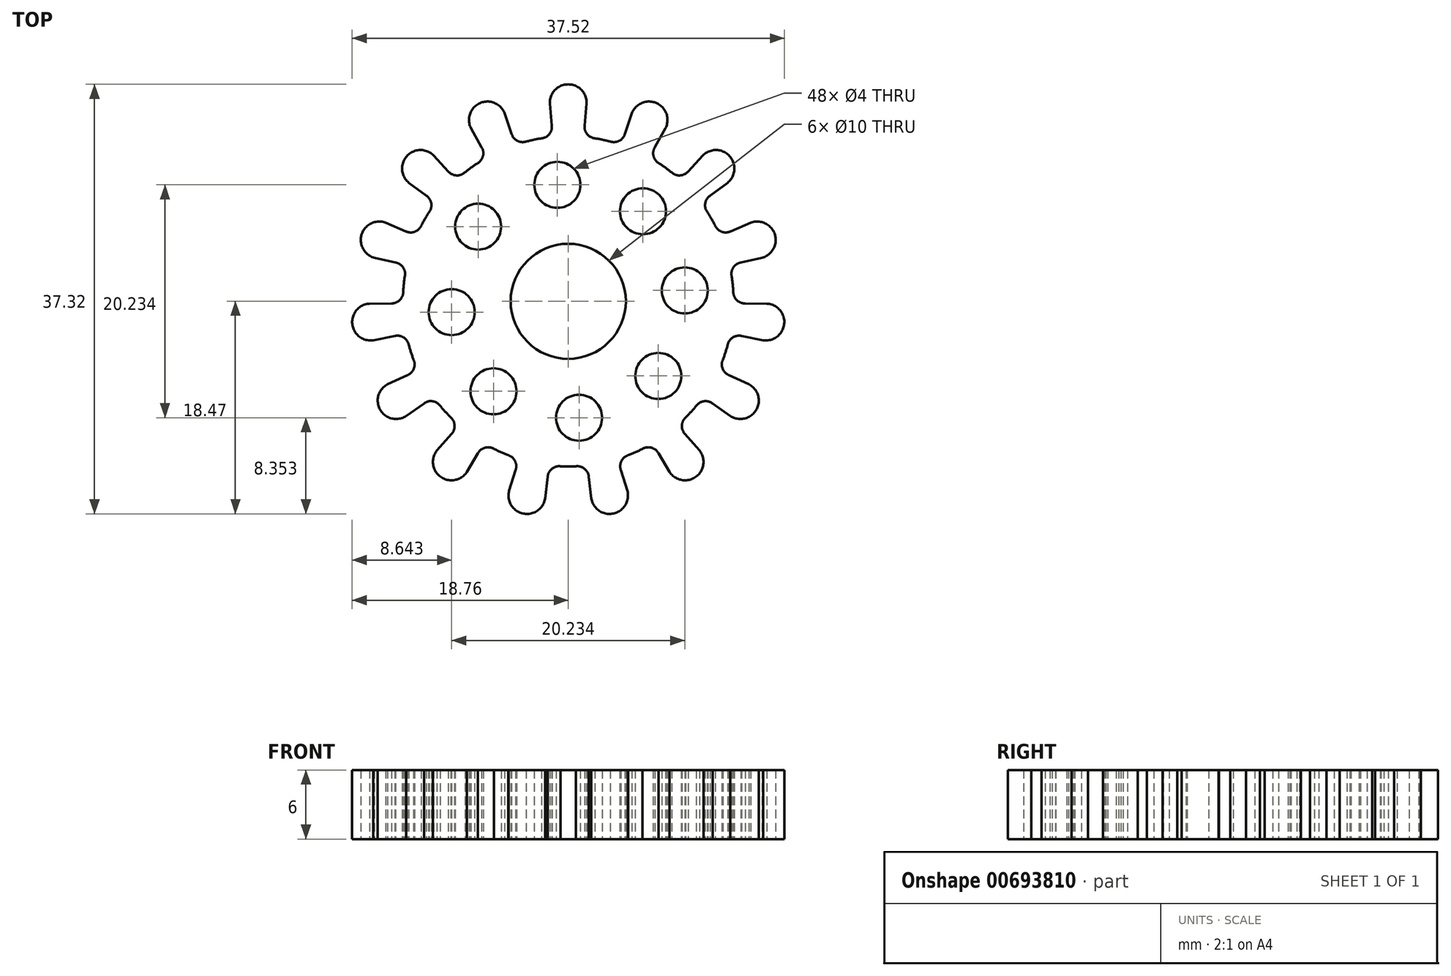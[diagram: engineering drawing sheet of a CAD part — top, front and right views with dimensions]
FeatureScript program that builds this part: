
annotation { "Feature Type Name" : "Feature", "Feature Type Description" : "" }
export const myFeature = defineFeature(function(context is Context, id is Id, definition is map)
    precondition{}
    {
        {
            var Q0;
            Q0=qCreatedBy(makeId("Top.planeOp"),FACE);
            var sketch = newSketch(context, id + "F0", { "sketchPlane" : qUnion([Q0])});
            skArc(sketch, "E0", {"start": v(1.6, 17.18) * mm, "mid": v(0, 18.85) * mm, "end": v(-1.6, 17.18) * mm});
            skPoint(sketch, "E1.center", {"position": v(0, 0) * mm});
            skLineSegment(sketch, "E2", {"start": v(1.6, 17.18) * mm, "end": v(1.42, 15.29) * mm});
            skArc(sketch, "E3", {"start": v(1.42, 15.29) * mm, "mid": v(1.63, 14.53) * mm, "end": v(2.32, 14.16) * mm});
            skCircle(sketch, "E4", {"center": v(0, 0) * mm, "radius": 17.25 * mm, "construction": true});
            skLineSegment(sketch, "E5.anchor1", {"start": v(0, 0) * mm, "end": v(-1.6, 17.18) * mm, "construction": true});
            skArc(sketch, "E6", {"start": v(3.64, 13.88) * mm, "mid": v(4.42, 13.94) * mm, "end": v(4.92, 14.54) * mm});
            skLineSegment(sketch, "E7", {"start": v(4.92, 14.54) * mm, "end": v(5.53, 16.34) * mm});
            skArc(sketch, "E8", {"start": v(2.32, 14.16) * mm, "mid": v(2.98, 14.04) * mm, "end": v(3.64, 13.88) * mm});
            skArc(sketch, "E9.1.0", {"start": v(8.45, 15.04) * mm, "mid": v(7.67, 17.22) * mm, "end": v(5.53, 16.34) * mm});
            skPoint(sketch, "E9.1.1", {"position": v(7.02, 15.76) * mm});
            skArc(sketch, "E9.1.2", {"start": v(8.97, 11.2) * mm, "mid": v(9.7, 10.94) * mm, "end": v(10.4, 11.28) * mm});
            skLineSegment(sketch, "E9.1.3", {"start": v(10.4, 11.28) * mm, "end": v(11.7, 12.68) * mm});
            skLineSegment(sketch, "E9.1.4", {"start": v(8.45, 15.04) * mm, "end": v(7.52, 13.39) * mm});
            skArc(sketch, "E9.1.5", {"start": v(7.52, 13.39) * mm, "mid": v(7.4, 12.61) * mm, "end": v(7.88, 12) * mm});
            skArc(sketch, "E9.1.6", {"start": v(7.88, 12) * mm, "mid": v(8.43, 11.6) * mm, "end": v(8.97, 11.2) * mm});
            skArc(sketch, "E9.2.0", {"start": v(13.83, 10.3) * mm, "mid": v(14, 12.61) * mm, "end": v(11.7, 12.68) * mm});
            skPoint(sketch, "E9.2.1", {"position": v(12.82, 11.54) * mm});
            skArc(sketch, "E9.2.2", {"start": v(12.75, 6.58) * mm, "mid": v(13.32, 6.04) * mm, "end": v(14.1, 6.08) * mm});
            skLineSegment(sketch, "E9.2.3", {"start": v(14.1, 6.08) * mm, "end": v(15.84, 6.83) * mm});
            skLineSegment(sketch, "E9.2.4", {"start": v(13.83, 10.3) * mm, "end": v(12.31, 9.17) * mm});
            skArc(sketch, "E9.2.5", {"start": v(12.31, 9.17) * mm, "mid": v(11.9, 8.51) * mm, "end": v(12.08, 7.75) * mm});
            skArc(sketch, "E9.2.6", {"start": v(12.08, 7.75) * mm, "mid": v(12.43, 7.17) * mm, "end": v(12.75, 6.58) * mm});
            skArc(sketch, "E9.3.0", {"start": v(16.83, 3.79) * mm, "mid": v(17.93, 5.82) * mm, "end": v(15.84, 6.83) * mm});
            skPoint(sketch, "E9.3.1", {"position": v(16.4, 5.33) * mm});
            skArc(sketch, "E9.3.2", {"start": v(14.33, 0.83) * mm, "mid": v(14.62, 0.1) * mm, "end": v(15.35, -0.18) * mm});
            skLineSegment(sketch, "E9.3.3", {"start": v(15.35, -0.18) * mm, "end": v(17.25, -0.2) * mm});
            skLineSegment(sketch, "E9.3.4", {"start": v(16.83, 3.79) * mm, "end": v(14.98, 3.37) * mm});
            skArc(sketch, "E9.3.5", {"start": v(14.98, 3.37) * mm, "mid": v(14.33, 2.94) * mm, "end": v(14.19, 2.17) * mm});
            skArc(sketch, "E9.3.6", {"start": v(14.19, 2.17) * mm, "mid": v(14.27, 1.5) * mm, "end": v(14.33, 0.83) * mm});
            skArc(sketch, "E9.4.0", {"start": v(16.91, -3.38) * mm, "mid": v(18.75, -1.97) * mm, "end": v(17.25, -0.2) * mm});
            skPoint(sketch, "E9.4.1", {"position": v(17.16, -1.8) * mm});
            skArc(sketch, "E9.4.2", {"start": v(13.42, -5.07) * mm, "mid": v(13.4, -5.85) * mm, "end": v(13.95, -6.41) * mm});
            skLineSegment(sketch, "E9.4.3", {"start": v(13.95, -6.41) * mm, "end": v(15.67, -7.2) * mm});
            skLineSegment(sketch, "E9.4.4", {"start": v(16.91, -3.38) * mm, "end": v(15.06, -3.01) * mm});
            skArc(sketch, "E9.4.5", {"start": v(15.06, -3.01) * mm, "mid": v(14.28, -3.14) * mm, "end": v(13.84, -3.79) * mm});
            skArc(sketch, "E9.4.6", {"start": v(13.84, -3.79) * mm, "mid": v(13.65, -4.43) * mm, "end": v(13.42, -5.07) * mm});
            skArc(sketch, "E9.5.0", {"start": v(14.08, -9.97) * mm, "mid": v(16.32, -9.43) * mm, "end": v(15.67, -7.2) * mm});
            skPoint(sketch, "E9.5.1", {"position": v(14.94, -8.63) * mm});
            skArc(sketch, "E9.5.2", {"start": v(10.2, -10.1) * mm, "mid": v(9.86, -10.8) * mm, "end": v(10.13, -11.53) * mm});
            skLineSegment(sketch, "E9.5.3", {"start": v(10.13, -11.53) * mm, "end": v(11.39, -12.96) * mm});
            skLineSegment(sketch, "E9.5.4", {"start": v(14.08, -9.97) * mm, "end": v(12.53, -8.88) * mm});
            skArc(sketch, "E9.5.5", {"start": v(12.53, -8.88) * mm, "mid": v(11.77, -8.68) * mm, "end": v(11.1, -9.1) * mm});
            skArc(sketch, "E9.5.6", {"start": v(11.1, -9.1) * mm, "mid": v(10.66, -9.6) * mm, "end": v(10.2, -10.1) * mm});
            skArc(sketch, "E9.6.0", {"start": v(8.8, -14.83) * mm, "mid": v(11.08, -15.25) * mm, "end": v(11.39, -12.96) * mm});
            skPoint(sketch, "E9.6.1", {"position": v(10.14, -13.96) * mm});
            skArc(sketch, "E9.6.2", {"start": v(5.21, -13.37) * mm, "mid": v(4.62, -13.87) * mm, "end": v(4.57, -14.65) * mm});
            skLineSegment(sketch, "E9.6.3", {"start": v(4.57, -14.65) * mm, "end": v(5.13, -16.47) * mm});
            skLineSegment(sketch, "E9.6.4", {"start": v(8.8, -14.83) * mm, "end": v(7.84, -13.2) * mm});
            skArc(sketch, "E9.6.5", {"start": v(7.84, -13.2) * mm, "mid": v(7.22, -12.72) * mm, "end": v(6.45, -12.82) * mm});
            skArc(sketch, "E9.6.6", {"start": v(6.45, -12.82) * mm, "mid": v(5.84, -13.1) * mm, "end": v(5.21, -13.37) * mm});
            skArc(sketch, "E9.7.0", {"start": v(2, -17.13) * mm, "mid": v(3.92, -18.44) * mm, "end": v(5.13, -16.47) * mm});
            skPoint(sketch, "E9.7.1", {"position": v(3.59, -16.87) * mm});
            skArc(sketch, "E9.7.2", {"start": v(-0.67, -14.33) * mm, "mid": v(-1.42, -14.55) * mm, "end": v(-1.79, -15.25) * mm});
            skLineSegment(sketch, "E9.7.3", {"start": v(-1.79, -15.25) * mm, "end": v(-2, -17.13) * mm});
            skLineSegment(sketch, "E9.7.4", {"start": v(2, -17.13) * mm, "end": v(1.79, -15.25) * mm});
            skArc(sketch, "E9.7.5", {"start": v(1.79, -15.25) * mm, "mid": v(1.43, -14.56) * mm, "end": v(0.67, -14.33) * mm});
            skArc(sketch, "E9.7.6", {"start": v(0.67, -14.33) * mm, "mid": v(0, -14.35) * mm, "end": v(-0.67, -14.33) * mm});
            skArc(sketch, "E9.8.0", {"start": v(-5.13, -16.47) * mm, "mid": v(-3.92, -18.44) * mm, "end": v(-2, -17.13) * mm});
            skPoint(sketch, "E9.8.1", {"position": v(-3.59, -16.87) * mm});
            skArc(sketch, "E9.8.2", {"start": v(-6.45, -12.82) * mm, "mid": v(-7.22, -12.72) * mm, "end": v(-7.83, -13.2) * mm});
            skLineSegment(sketch, "E9.8.3", {"start": v(-7.83, -13.2) * mm, "end": v(-8.8, -14.83) * mm});
            skLineSegment(sketch, "E9.8.4", {"start": v(-5.13, -16.47) * mm, "end": v(-4.57, -14.66) * mm});
            skArc(sketch, "E9.8.5", {"start": v(-4.57, -14.66) * mm, "mid": v(-4.62, -13.88) * mm, "end": v(-5.21, -13.37) * mm});
            skArc(sketch, "E9.8.6", {"start": v(-5.21, -13.37) * mm, "mid": v(-5.84, -13.1) * mm, "end": v(-6.45, -12.82) * mm});
            skLineSegment(sketch, "E9.anchor2", {"start": v(0, 0) * mm, "end": v(-2, -17.13) * mm, "construction": true});
            skArc(sketch, "E10.1.0", {"start": v(-11.39, -12.96) * mm, "mid": v(-11.08, -15.25) * mm, "end": v(-8.8, -14.83) * mm});
            skLineSegment(sketch, "E10.1.1", {"start": v(-11.39, -12.96) * mm, "end": v(-10.14, -11.53) * mm});
            skArc(sketch, "E10.1.2", {"start": v(-10.14, -11.53) * mm, "mid": v(-9.86, -10.8) * mm, "end": v(-10.2, -10.1) * mm});
            skArc(sketch, "E10.1.3", {"start": v(-10.2, -10.1) * mm, "mid": v(-10.66, -9.6) * mm, "end": v(-11.1, -9.1) * mm});
            skArc(sketch, "E10.1.4", {"start": v(-11.1, -9.1) * mm, "mid": v(-11.77, -8.68) * mm, "end": v(-12.53, -8.87) * mm});
            skLineSegment(sketch, "E10.1.5", {"start": v(-12.53, -8.87) * mm, "end": v(-14.08, -9.97) * mm});
            skArc(sketch, "E10.2.0", {"start": v(-15.67, -7.2) * mm, "mid": v(-16.32, -9.42) * mm, "end": v(-14.08, -9.97) * mm});
            skLineSegment(sketch, "E10.2.1", {"start": v(-15.67, -7.2) * mm, "end": v(-13.95, -6.41) * mm});
            skArc(sketch, "E10.2.2", {"start": v(-13.95, -6.41) * mm, "mid": v(-13.4, -5.85) * mm, "end": v(-13.42, -5.07) * mm});
            skArc(sketch, "E10.2.3", {"start": v(-13.42, -5.07) * mm, "mid": v(-13.65, -4.43) * mm, "end": v(-13.84, -3.79) * mm});
            skArc(sketch, "E10.2.4", {"start": v(-13.84, -3.79) * mm, "mid": v(-14.28, -3.14) * mm, "end": v(-15.05, -3.01) * mm});
            skLineSegment(sketch, "E10.2.5", {"start": v(-15.05, -3.01) * mm, "end": v(-16.91, -3.38) * mm});
            skArc(sketch, "E10.3.0", {"start": v(-17.25, -0.2) * mm, "mid": v(-18.75, -1.97) * mm, "end": v(-16.91, -3.38) * mm});
            skLineSegment(sketch, "E10.3.1", {"start": v(-17.25, -0.2) * mm, "end": v(-15.35, -0.18) * mm});
            skArc(sketch, "E10.3.2", {"start": v(-15.35, -0.18) * mm, "mid": v(-14.62, 0.1) * mm, "end": v(-14.33, 0.83) * mm});
            skArc(sketch, "E10.3.3", {"start": v(-14.33, 0.83) * mm, "mid": v(-14.27, 1.5) * mm, "end": v(-14.19, 2.17) * mm});
            skArc(sketch, "E10.3.4", {"start": v(-14.19, 2.17) * mm, "mid": v(-14.33, 2.94) * mm, "end": v(-14.98, 3.37) * mm});
            skLineSegment(sketch, "E10.3.5", {"start": v(-14.98, 3.37) * mm, "end": v(-16.83, 3.79) * mm});
            skArc(sketch, "E10.4.0", {"start": v(-15.84, 6.83) * mm, "mid": v(-17.93, 5.82) * mm, "end": v(-16.83, 3.79) * mm});
            skLineSegment(sketch, "E10.4.1", {"start": v(-15.84, 6.83) * mm, "end": v(-14.1, 6.08) * mm});
            skArc(sketch, "E10.4.2", {"start": v(-14.1, 6.08) * mm, "mid": v(-13.32, 6.04) * mm, "end": v(-12.75, 6.58) * mm});
            skArc(sketch, "E10.4.3", {"start": v(-12.75, 6.58) * mm, "mid": v(-12.43, 7.18) * mm, "end": v(-12.08, 7.75) * mm});
            skArc(sketch, "E10.4.4", {"start": v(-12.08, 7.75) * mm, "mid": v(-11.9, 8.5) * mm, "end": v(-12.3, 9.17) * mm});
            skLineSegment(sketch, "E10.4.5", {"start": v(-12.3, 9.17) * mm, "end": v(-13.83, 10.3) * mm});
            skArc(sketch, "E10.5.0", {"start": v(-11.7, 12.68) * mm, "mid": v(-14, 12.61) * mm, "end": v(-13.83, 10.3) * mm});
            skLineSegment(sketch, "E10.5.1", {"start": v(-11.7, 12.68) * mm, "end": v(-10.4, 11.29) * mm});
            skArc(sketch, "E10.5.2", {"start": v(-10.4, 11.29) * mm, "mid": v(-9.7, 10.94) * mm, "end": v(-8.97, 11.2) * mm});
            skArc(sketch, "E10.5.3", {"start": v(-8.97, 11.2) * mm, "mid": v(-8.43, 11.6) * mm, "end": v(-7.88, 12) * mm});
            skArc(sketch, "E10.5.4", {"start": v(-7.88, 12) * mm, "mid": v(-7.4, 12.61) * mm, "end": v(-7.52, 13.38) * mm});
            skLineSegment(sketch, "E10.5.5", {"start": v(-7.52, 13.38) * mm, "end": v(-8.45, 15.04) * mm});
            skArc(sketch, "E10.6.0", {"start": v(-5.53, 16.34) * mm, "mid": v(-7.67, 17.22) * mm, "end": v(-8.45, 15.04) * mm});
            skLineSegment(sketch, "E10.6.1", {"start": v(-5.53, 16.34) * mm, "end": v(-4.92, 14.55) * mm});
            skArc(sketch, "E10.6.2", {"start": v(-4.92, 14.55) * mm, "mid": v(-4.42, 13.94) * mm, "end": v(-3.64, 13.88) * mm});
            skArc(sketch, "E10.6.3", {"start": v(-3.64, 13.88) * mm, "mid": v(-2.98, 14.04) * mm, "end": v(-2.32, 14.16) * mm});
            skArc(sketch, "E10.6.4", {"start": v(-2.32, 14.16) * mm, "mid": v(-1.63, 14.53) * mm, "end": v(-1.42, 15.28) * mm});
            skLineSegment(sketch, "E10.6.5", {"start": v(-1.42, 15.28) * mm, "end": v(-1.6, 17.18) * mm});
            skLineSegment(sketch, "E10.anchor1", {"start": v(0, 0) * mm, "end": v(-8.8, -14.83) * mm, "construction": true});
            skCircle(sketch, "E11", {"center": v(0, 0) * mm, "radius": 5 * mm});
            skCircle(sketch, "E12", {"center": v(-0.94, 10.12) * mm, "radius": 2 * mm});
            skCircle(sketch, "E13.1.0", {"center": v(-7.82, 6.49) * mm, "radius": 2 * mm});
            skCircle(sketch, "E13.2.0", {"center": v(-10.12, -0.94) * mm, "radius": 2 * mm});
            skCircle(sketch, "E13.3.0", {"center": v(-6.49, -7.82) * mm, "radius": 2 * mm});
            skCircle(sketch, "E13.4.0", {"center": v(0.94, -10.12) * mm, "radius": 2 * mm});
            skCircle(sketch, "E13.5.0", {"center": v(7.82, -6.49) * mm, "radius": 2 * mm});
            skCircle(sketch, "E13.6.0", {"center": v(10.12, 0.94) * mm, "radius": 2 * mm});
            skCircle(sketch, "E13.7.0", {"center": v(6.49, 7.82) * mm, "radius": 2 * mm});
            skSolve(sketch);
        }
        {
            var Q0;
            Q0 = qSketchRegion(id + "F0", true);
            extrude(context, id + "F1", {"entities" : qUnion([Q0]), "depth" : 6 * mm, "offsetDistance" : 25 * mm});
        }
    });
